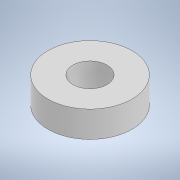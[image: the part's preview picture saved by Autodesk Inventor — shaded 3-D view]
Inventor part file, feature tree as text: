
AUTODESK INVENTOR PART (.ipt)
format: ipt  version: 2022 (Build 260153000, 153)  size: 96,768 bytes
history: native  units: mm
features: extrude x1, sketch x1
ambient origin geometry x8: Origin, YZ Plane, XZ Plane, XY Plane, X Axis, Y Axis, Z Axis, Center Point
bodies: Solid1 (feature_tree)
feature tree (2):
  extrude  "Extrusion1"  Depth=10.0mm
  sketch  "Sketch1"  dims[d0=13.0mm d1=32.0mm d2=10.0mm d3=0.0mm]
